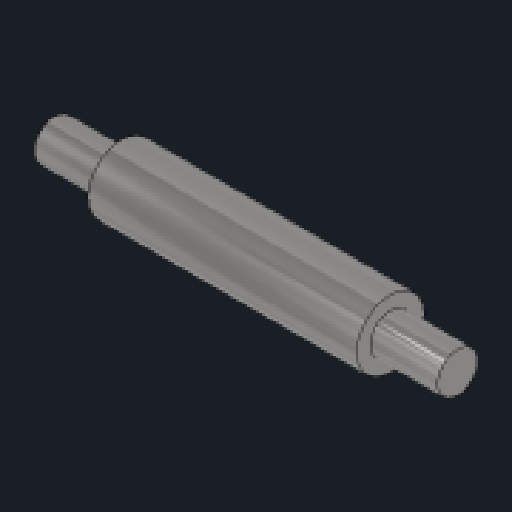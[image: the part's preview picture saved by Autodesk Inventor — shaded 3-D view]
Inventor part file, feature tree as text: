
AUTODESK INVENTOR PART (.ipt)
format: ipt  version: 2023.2 (Build 272271030, 271C)  size: 102,912 bytes
history: native  units: mm
features: revolve x1, sketch x1
ambient origin geometry x8: Origin, YZ Plane, XZ Plane, XY Plane, X Axis, Y Axis, Z Axis, Center Point
bodies: Body1 (feature_tree)
feature tree (2):
  revolve  "Revolution1"  [1 undecoded]
  sketch  "Sketch2"  dims[d3=30.0mm d4=2.5mm d5=1.5mm d6=5.0mm d7=90.0deg]
note: 1 required parameter value undecoded (feature->parameter linkage not recoverable at this tier; creation-order binding heuristic only, values carry confidence <= 0.55)
